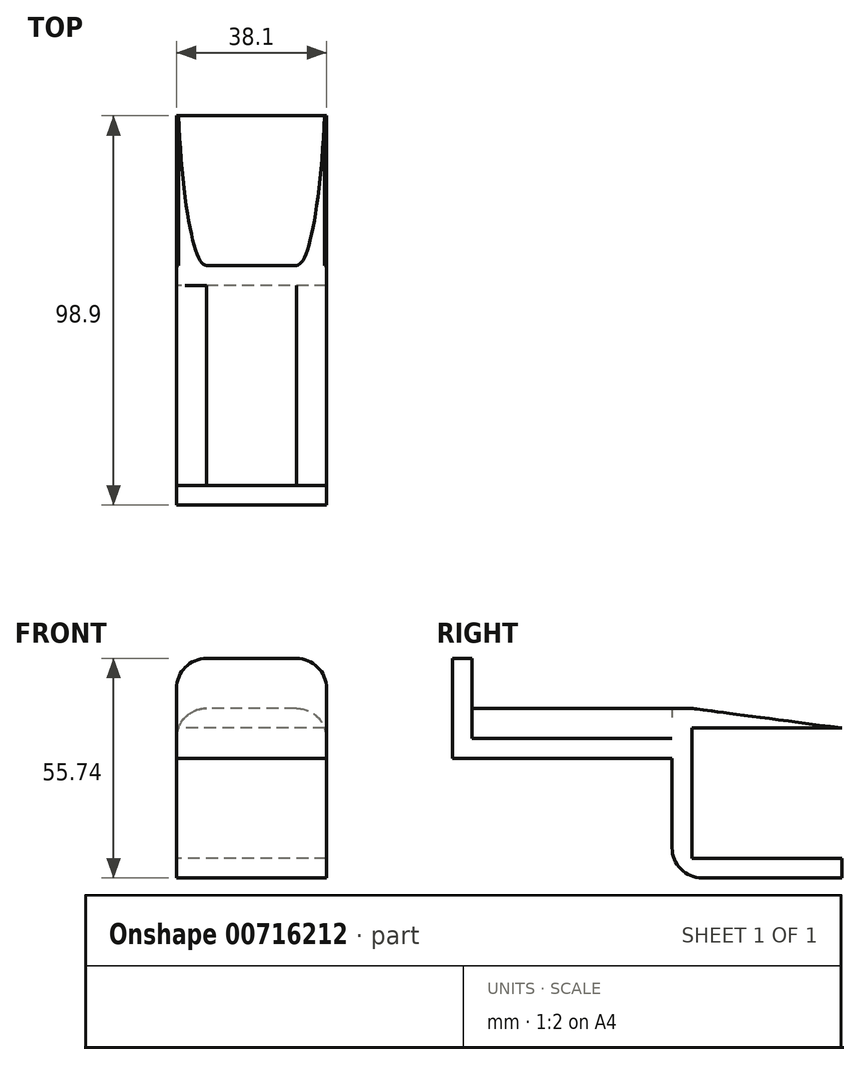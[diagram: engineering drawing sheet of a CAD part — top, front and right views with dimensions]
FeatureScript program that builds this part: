
annotation { "Feature Type Name" : "Feature", "Feature Type Description" : "" }
export const myFeature = defineFeature(function(context is Context, id is Id, definition is map)
    precondition{}
    {
        {
            var Q0;
            Q0=qCreatedBy(makeId("Front.planeOp"),FACE);
            var sketch = newSketch(context, id + "F0", { "sketchPlane" : qUnion([Q0])});
            skLineSegment(sketch, "E0.bottom", {"start": v(19.05, -21.52) * mm, "end": v(-19.05, -21.52) * mm});
            skLineSegment(sketch, "E0.top", {"start": v(19.05, 21.52) * mm, "end": v(-19.05, 21.52) * mm});
            skLineSegment(sketch, "E0.left", {"start": v(19.05, -21.52) * mm, "end": v(19.05, 21.52) * mm});
            skLineSegment(sketch, "E0.right", {"start": v(-19.05, -21.52) * mm, "end": v(-19.05, 21.52) * mm});
            skPoint(sketch, "E0.middle", {"position": v(0, 0) * mm});
            skSolve(sketch);
        }
        {
            var Q0;
            Q0 = qSketchRegion(id + "F0", true);
            extrude(context, id + "F1", {"entities" : qUnion([Q0]), "depth" : 5 * mm, "offsetDistance" : 25.4 * mm});
        }
        {
            var Q0;
            Q0=makeQuery(id+"F1.opExtrude","CAP_FACE",FACE,{"disambiguationData":[OSD([sQuery(id+"F0.wireOp",EDGE,"E0.bottom"),sQuery(id+"F0.wireOp",EDGE,"E0.top"),sQuery(id+"F0.wireOp",EDGE,"E0.left"),sQuery(id+"F0.wireOp",EDGE,"E0.right")])],"isStart":true});
            var sketch = newSketch(context, id + "F2", { "sketchPlane" : qUnion([Q0])});
            skLineSegment(sketch, "E1.bottom", {"start": v(-19.05, 21.52) * mm, "end": v(19.05, 21.52) * mm});
            skLineSegment(sketch, "E1.top", {"start": v(-19.05, 16.52) * mm, "end": v(19.05, 16.52) * mm});
            skLineSegment(sketch, "E1.left", {"start": v(-19.05, 21.52) * mm, "end": v(-19.05, 16.52) * mm});
            skLineSegment(sketch, "E1.right", {"start": v(19.05, 21.52) * mm, "end": v(19.05, 16.52) * mm});
            skLineSegment(sketch, "E2.bottom", {"start": v(-19.05, -21.52) * mm, "end": v(19.05, -21.52) * mm});
            skLineSegment(sketch, "E2.top", {"start": v(-19.05, -16.52) * mm, "end": v(19.05, -16.52) * mm});
            skLineSegment(sketch, "E2.left", {"start": v(-19.05, -21.52) * mm, "end": v(-19.05, -16.52) * mm});
            skLineSegment(sketch, "E2.right", {"start": v(19.05, -21.52) * mm, "end": v(19.05, -16.52) * mm});
            skSolve(sketch);
        }
        {
            var Q0;
            Q0 = qSketchRegion(id + "F2", true);
            extrude(context, id + "F3", {"entities" : qUnion([Q0]), "operationType" : NewBodyOperationType.ADD, "depth" : 38.1 * mm, "offsetDistance" : 25.4 * mm});
        }
        {
            var Q0;
            Q0=makeQuery(id+"F3.boolean.opBoolean","MERGE",FACE,{"derivedFrom":[makeQuery(id+"F1.opExtrude","SWEPT_FACE",FACE,{"disambiguationData":[OSD([sQuery(id+"F0.wireOp",EDGE,"E0.left")])]}),makeQuery(id+"F3.opExtrude","SWEPT_FACE",FACE,{"disambiguationData":[OSD([sQuery(id+"F2.wireOp",EDGE,"E1.left")])]}),makeQuery(id+"F3.opExtrude","SWEPT_FACE",FACE,{"disambiguationData":[OSD([sQuery(id+"F2.wireOp",EDGE,"E2.left")])]})]});
            var sketch = newSketch(context, id + "F4", { "sketchPlane" : qUnion([Q0])});
            skLineSegment(sketch, "E3", {"start": v(38.1, 16.52) * mm, "end": v(0, 21.52) * mm});
            skLineSegment(sketch, "E4", {"start": v(0, 21.52) * mm, "end": v(38.1, 21.52) * mm});
            skLineSegment(sketch, "E5", {"start": v(38.1, 21.52) * mm, "end": v(38.1, 16.52) * mm});
            skSolve(sketch);
        }
        {
            var Q0;
            Q0 = qSketchRegion(id + "F4", true);
            extrude(context, id + "F5", {"entities" : qUnion([Q0]), "operationType" : NewBodyOperationType.REMOVE, "endBound" : BoundingType.UP_TO_NEXT, "oppositeDirection" : true, "depth" : 25.4 * mm, "offsetDistance" : 25.4 * mm});
        }
        {
            var Q0;
            Q0=makeQuery(id+"F5.boolean.opBoolean","COPY",EDGE,{"derivedFrom":makeQuery(id+"F5.opExtrude","TWEAK_EDGE",EDGE,{"derivedFrom":[makeQuery(id+"F3.boolean.opBoolean","MERGE",FACE,{"derivedFrom":[makeQuery(id+"F1.opExtrude","SWEPT_FACE",FACE,{"disambiguationData":[OSD([sQuery(id+"F0.wireOp",EDGE,"E0.right")])]}),makeQuery(id+"F3.opExtrude","SWEPT_FACE",FACE,{"disambiguationData":[OSD([sQuery(id+"F2.wireOp",EDGE,"E1.right")])]}),makeQuery(id+"F3.opExtrude","SWEPT_FACE",FACE,{"disambiguationData":[OSD([sQuery(id+"F2.wireOp",EDGE,"E2.right")])]})]}),makeQuery(id+"F4.imprint","IMPRINT",EDGE,{"derivedFrom":sQuery(id+"F4.wireOp",EDGE,"E3")})]})});
            var Q1;
            Q1=makeQuery(id+"F3.boolean.opBoolean","MERGE",EDGE,{"derivedFrom":[makeQuery(id+"F1.opExtrude","SWEPT_EDGE",EDGE,{"disambiguationData":[OSD([sQuery(id+"F0.wireOp",EDGE,"E0.top"),sQuery(id+"F0.wireOp",EDGE,"E0.right")])]}),makeQuery(id+"F3.opExtrude","SWEPT_EDGE",EDGE,{"disambiguationData":[OSD([sQuery(id+"F2.wireOp",EDGE,"E1.bottom"),sQuery(id+"F2.wireOp",EDGE,"E1.right")])]})]});
            var Q2;
            Q2=makeQuery(id+"F5.boolean.opBoolean","COPY",EDGE,{"derivedFrom":makeQuery(id+"F5.opExtrude","CAP_EDGE",EDGE,{"disambiguationData":[OSD([sQuery(id+"F4.wireOp",EDGE,"E3")])],"isStart":true})});
            var Q3;
            Q3=makeQuery(id+"F3.boolean.opBoolean","MERGE",EDGE,{"derivedFrom":[makeQuery(id+"F1.opExtrude","SWEPT_EDGE",EDGE,{"disambiguationData":[OSD([sQuery(id+"F0.wireOp",EDGE,"E0.top"),sQuery(id+"F0.wireOp",EDGE,"E0.left")])]}),makeQuery(id+"F3.opExtrude","SWEPT_EDGE",EDGE,{"disambiguationData":[OSD([sQuery(id+"F2.wireOp",EDGE,"E1.bottom"),sQuery(id+"F2.wireOp",EDGE,"E1.left")])]})]});
            fillet(context, id + "F6", {"entities" : qUnion([Q0, Q1, Q2, Q3]), "radius" : 7.62 * mm, "tangentPropagation" : true, "allowEdgeOverflow" : false});
        }
        {
            var Q0;
            Q0=makeQuery(id+"F1.opExtrude","CAP_FACE",FACE,{"disambiguationData":[OSD([sQuery(id+"F0.wireOp",EDGE,"E0.bottom"),sQuery(id+"F0.wireOp",EDGE,"E0.top"),sQuery(id+"F0.wireOp",EDGE,"E0.left"),sQuery(id+"F0.wireOp",EDGE,"E0.right")])],"isStart":false});
            var sketch = newSketch(context, id + "F7", { "sketchPlane" : qUnion([Q0])});
            skFitSpline(sketch, "E6", {"points": [v(-19.05, 13.9) * mm, v(-16.82, 19.29) * mm, v(-11.43, 21.52) * mm], "startDerivative": vector(0.12, 12.67) * mm, "endDerivative": vector(12.7, 0.22) * mm});
            skFitSpline(sketch, "E7", {"points": [v(11.43, 21.52) * mm, v(16.82, 19.29) * mm, v(19.05, 13.9) * mm], "startDerivative": vector(11.03, 0.42) * mm, "endDerivative": vector(0.16, -11.76) * mm});
            skLineSegment(sketch, "E8", {"start": v(-19.05, 13.9) * mm, "end": v(-19.05, 8.82) * mm});
            skLineSegment(sketch, "E9", {"start": v(-19.05, 8.82) * mm, "end": v(19.05, 8.82) * mm});
            skLineSegment(sketch, "E10", {"start": v(19.05, 8.82) * mm, "end": v(19.05, 13.9) * mm});
            skLineSegment(sketch, "E11", {"start": v(11.43, 21.52) * mm, "end": v(-11.43, 21.52) * mm});
            skSolve(sketch);
        }
        {
            var Q0;
            Q0 = qSketchRegion(id + "F7", true);
            extrude(context, id + "F8", {"entities" : qUnion([Q0]), "operationType" : NewBodyOperationType.ADD, "depth" : 50.8 * mm, "offsetDistance" : 25.4 * mm});
        }
        {
            var Q0;
            Q0=makeQuery(id+"F8.opExtrude","CAP_FACE",FACE,{"disambiguationData":[OSD([sQuery(id+"F7.wireOp",EDGE,"E6"),sQuery(id+"F7.wireOp",EDGE,"E7"),sQuery(id+"F7.wireOp",EDGE,"E8"),sQuery(id+"F7.wireOp",EDGE,"E9"),sQuery(id+"F7.wireOp",EDGE,"E10"),sQuery(id+"F7.wireOp",EDGE,"E11")])],"isStart":false});
            var sketch = newSketch(context, id + "F9", { "sketchPlane" : qUnion([Q0])});
            skLineSegment(sketch, "E12.bottom", {"start": v(-19.05, 8.82) * mm, "end": v(19.05, 8.82) * mm});
            skLineSegment(sketch, "E12.top", {"start": v(-19.05, 34.22) * mm, "end": v(19.05, 34.22) * mm});
            skLineSegment(sketch, "E12.left", {"start": v(-19.05, 8.82) * mm, "end": v(-19.05, 34.22) * mm});
            skLineSegment(sketch, "E12.right", {"start": v(19.05, 8.82) * mm, "end": v(19.05, 34.22) * mm});
            skSolve(sketch);
        }
        {
            var Q0;
            Q0 = qSketchRegion(id + "F9", true);
            extrude(context, id + "F10", {"entities" : qUnion([Q0]), "operationType" : NewBodyOperationType.ADD, "depth" : 5 * mm, "offsetDistance" : 25.4 * mm});
        }
        {
            var Q0;
            Q0=makeQuery(id+"F10.opExtrude","SWEPT_EDGE",EDGE,{"disambiguationData":[OSD([sQuery(id+"F9.wireOp",EDGE,"E12.top"),sQuery(id+"F9.wireOp",EDGE,"E12.left")])]});
            var Q1;
            Q1=makeQuery(id+"F10.opExtrude","SWEPT_EDGE",EDGE,{"disambiguationData":[OSD([sQuery(id+"F9.wireOp",EDGE,"E12.top"),sQuery(id+"F9.wireOp",EDGE,"E12.right")])]});
            fillet(context, id + "F11", {"entities" : qUnion([Q0, Q1]), "radius" : 7.62 * mm, "tangentPropagation" : true, "allowEdgeOverflow" : false});
        }
        {
            var Q0;
            Q0=makeQuery(id+"F1.opExtrude","CAP_EDGE",EDGE,{"disambiguationData":[OSD([sQuery(id+"F0.wireOp",EDGE,"E0.bottom")])],"isStart":false});
            fillet(context, id + "F12", {"entities" : qUnion([Q0]), "radius" : 7.62 * mm, "tangentPropagation" : true, "allowEdgeOverflow" : false});
        }
    });
